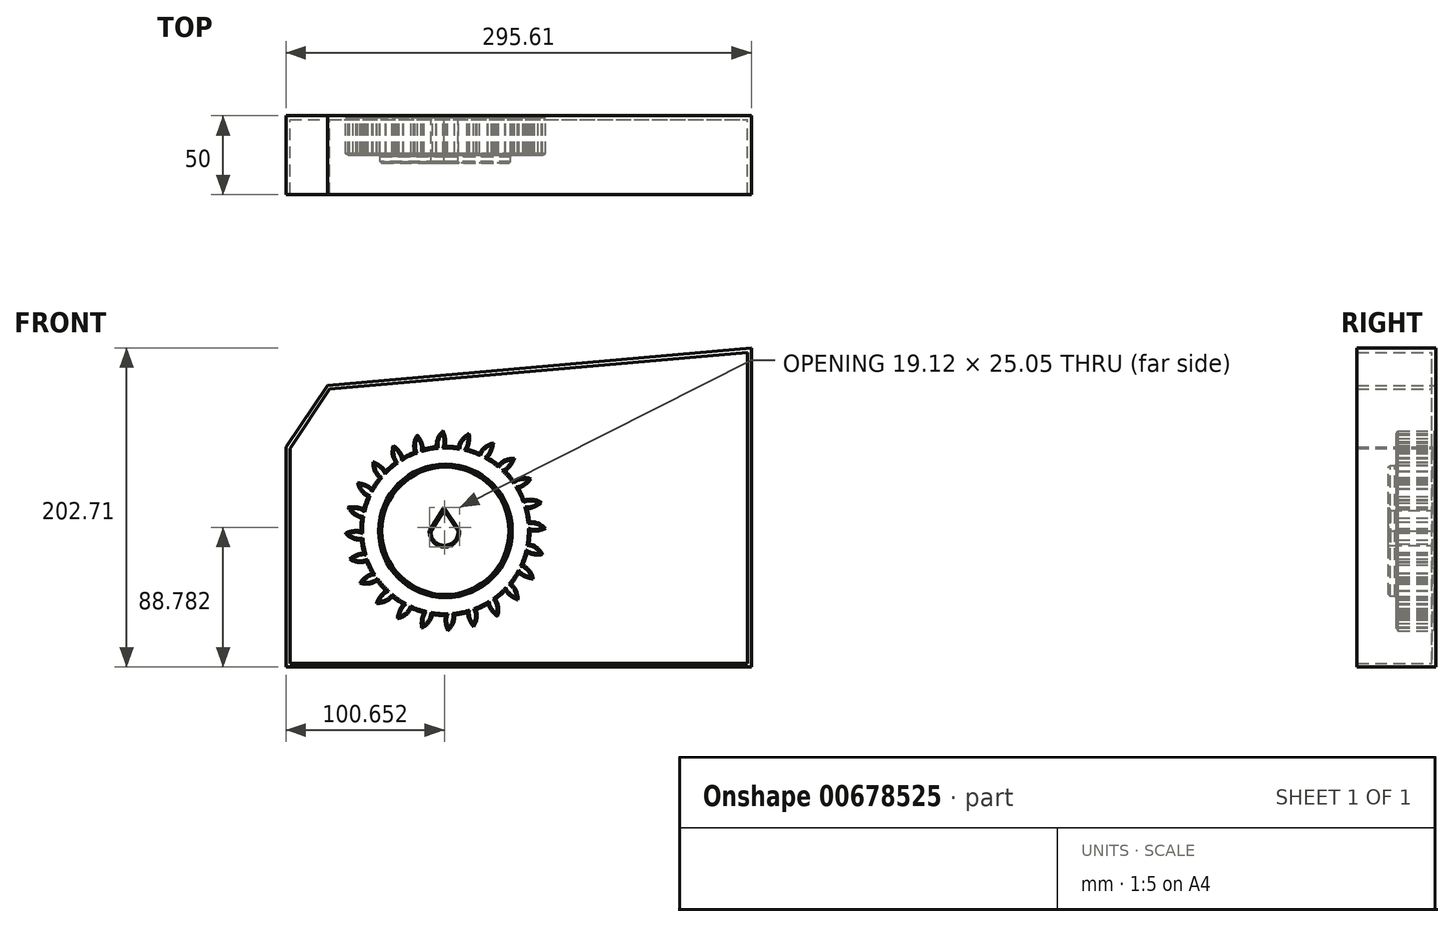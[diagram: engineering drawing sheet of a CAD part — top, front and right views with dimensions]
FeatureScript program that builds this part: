
annotation { "Feature Type Name" : "Feature", "Feature Type Description" : "" }
export const myFeature = defineFeature(function(context is Context, id is Id, definition is map)
    precondition{}
    {
        {
            var Q0;
            Q0=qCreatedBy(makeId("Front.planeOp"),FACE);
            var sketch = newSketch(context, id + "F0", { "sketchPlane" : qUnion([Q0])});
            skCircle(sketch, "E0", {"center": v(0, 0) * mm, "radius": 53.72 * mm});
            skCircle(sketch, "E1", {"center": v(0, 0) * mm, "radius": 58.67 * mm, "construction": true});
            skCircle(sketch, "E2", {"center": v(0, 0) * mm, "radius": 63.5 * mm, "construction": true});
            skLineSegment(sketch, "E3", {"start": v(0, 0) * mm, "end": v(0, 86.11) * mm, "construction": true});
            skLineSegment(sketch, "E4", {"start": v(0, 0) * mm, "end": v(-5.95, 90.7) * mm, "construction": true});
            skCircle(sketch, "E5", {"center": v(0, 58.67) * mm, "radius": 14.6 * mm, "construction": true});
            skLineSegment(sketch, "E6", {"start": v(0, 58.67) * mm, "end": v(-66.92, 58.67) * mm, "construction": true});
            skLineSegment(sketch, "E7", {"start": v(0, 58.67) * mm, "end": v(-68.71, 43.32) * mm, "construction": true});
            skCircle(sketch, "E8", {"center": v(-14.5, 56.86) * mm, "radius": 14.6 * mm, "construction": true});
            skArc(sketch, "E9", {"start": v(0, 58.67) * mm, "mid": v(-0.53, 61.14) * mm, "end": v(-1.48, 63.48) * mm});
            skArc(sketch, "E10", {"start": v(-0.23, 53.72) * mm, "mid": v(0.19, 56.18) * mm, "end": v(0, 58.67) * mm});
            skArc(sketch, "E11", {"start": v(-1.48, 63.48) * mm, "mid": v(-4.9, 58.99) * mm, "end": v(-5.76, 53.41) * mm});
            skCircle(sketch, "E12", {"center": v(0, 0) * mm, "radius": 41.43 * mm});
            skLineSegment(sketch, "E13", {"start": v(-9.22, 0) * mm, "end": v(-0.85, 12.95) * mm});
            skLineSegment(sketch, "E14", {"start": v(-0.85, 12.95) * mm, "end": v(7.96, 0) * mm});
            skArc(sketch, "E15", {"start": v(-9.22, 0) * mm, "mid": v(-0.63, -9.3) * mm, "end": v(7.96, 0) * mm});
            skSolve(sketch);
        }
        {
            var Q0;
            {var subQ0=sQuery(id+"F0.wireOp",EDGE,"E0");var subQ1=makeQuery(id+"F0.imprint","INTERSECT",VERTEX,{"derivedFrom":[subQ0,sQuery(id+"F0.wireOp",EDGE,"E10")]});Q0=makeQuery(id+"F0.imprint","IMPRINT",FACE,{"disambiguationData":[TD([[makeQuery(id+"F0.imprint","IMPRINT",EDGE,{"disambiguationData":[TD([[subQ1,-1.0]])],"derivedFrom":subQ0}),1.0]])]});}
            var Q1;
            Q1=makeQuery(id+"F0.imprint","IMPRINT",FACE,{"disambiguationData":[TD([[makeQuery(id+"F0.imprint","IMPRINT",EDGE,{"derivedFrom":sQuery(id+"F0.wireOp",EDGE,"E9")}),1.0]])]});
            extrude(context, id + "F1", {"entities" : qUnion([Q0, Q1]), "depth" : 25 * mm, "offsetDistance" : 25 * mm});
        }
        {
            var Q0;
            Q0=makeQuery(id+"F1.opExtrude","SWEPT_BODY",BODY,{"disambiguationData":[OSD([sQuery(id+"F0.wireOp",EDGE,"E0"),sQuery(id+"F0.wireOp",EDGE,"E9"),sQuery(id+"F0.wireOp",EDGE,"E10"),sQuery(id+"F0.wireOp",EDGE,"E11")])]});
            var Q1;
            Q1=makeQuery(id+"F1.opExtrude","SWEPT_FACE",FACE,{"disambiguationData":[OSD([sQuery(id+"F0.wireOp",EDGE,"E0")])]});
            circularPattern(context, id + "F2", {"entities" : qUnion([Q0]), "axis" : qUnion([Q1]), "angle" : 360 * degree, "instanceCount" : 24, "equalSpace" : true});
        }
        {
            var Q0;
            Q0=makeQuery(id+"F0.imprint","IMPRINT",FACE,{"disambiguationData":[TD([[makeQuery(id+"F0.imprint","IMPRINT",EDGE,{"derivedFrom":sQuery(id+"F0.wireOp",EDGE,"E12")}),1.0]])]});
            extrude(context, id + "F3", {"entities" : qUnion([Q0]), "operationType" : NewBodyOperationType.ADD, "depth" : 30 * mm, "offsetDistance" : 25 * mm});
        }
        {
            var Q0;
            Q0=makeQuery(id+"F3.opExtrude","CAP_FACE",FACE,{"disambiguationData":[OSD([sQuery(id+"F0.wireOp",EDGE,"E12"),sQuery(id+"F0.wireOp",EDGE,"E13"),sQuery(id+"F0.wireOp",EDGE,"E14"),sQuery(id+"F0.wireOp",EDGE,"E15")])],"isStart":false});
            chamfer(context, id + "F4", {"entities" : qUnion([Q0]), "width" : 1 * mm, "tangentPropagation" : true});
        }
        {
            var Q0;
            {var subQ0=makeQuery(id+"F1.opExtrude","CAP_FACE",FACE,{"disambiguationData":[OSD([sQuery(id+"F0.wireOp",EDGE,"E0"),sQuery(id+"F0.wireOp",EDGE,"E9"),sQuery(id+"F0.wireOp",EDGE,"E10"),sQuery(id+"F0.wireOp",EDGE,"E11"),sQuery(id+"F0.wireOp",EDGE,"E12")])],"isStart":false});Q0=makeQuery(id+"F3.boolean.opBoolean","MERGE",FACE,{"derivedFrom":[subQ0,makeQuery(id+"F2.opPattern","COPY",FACE,{"derivedFrom":subQ0,"instanceName":"1"}),makeQuery(id+"F2.opPattern","COPY",FACE,{"derivedFrom":subQ0,"instanceName":"2"}),makeQuery(id+"F2.opPattern","COPY",FACE,{"derivedFrom":subQ0,"instanceName":"3"}),makeQuery(id+"F2.opPattern","COPY",FACE,{"derivedFrom":subQ0,"instanceName":"4"}),makeQuery(id+"F2.opPattern","COPY",FACE,{"derivedFrom":subQ0,"instanceName":"5"}),makeQuery(id+"F2.opPattern","COPY",FACE,{"derivedFrom":subQ0,"instanceName":"6"}),makeQuery(id+"F2.opPattern","COPY",FACE,{"derivedFrom":subQ0,"instanceName":"7"}),makeQuery(id+"F2.opPattern","COPY",FACE,{"derivedFrom":subQ0,"instanceName":"8"}),makeQuery(id+"F2.opPattern","COPY",FACE,{"derivedFrom":subQ0,"instanceName":"9"}),makeQuery(id+"F2.opPattern","COPY",FACE,{"derivedFrom":subQ0,"instanceName":"10"}),makeQuery(id+"F2.opPattern","COPY",FACE,{"derivedFrom":subQ0,"instanceName":"11"}),makeQuery(id+"F2.opPattern","COPY",FACE,{"derivedFrom":subQ0,"instanceName":"12"}),makeQuery(id+"F2.opPattern","COPY",FACE,{"derivedFrom":subQ0,"instanceName":"13"}),makeQuery(id+"F2.opPattern","COPY",FACE,{"derivedFrom":subQ0,"instanceName":"14"}),makeQuery(id+"F2.opPattern","COPY",FACE,{"derivedFrom":subQ0,"instanceName":"15"}),makeQuery(id+"F2.opPattern","COPY",FACE,{"derivedFrom":subQ0,"instanceName":"16"}),makeQuery(id+"F2.opPattern","COPY",FACE,{"derivedFrom":subQ0,"instanceName":"17"}),makeQuery(id+"F2.opPattern","COPY",FACE,{"derivedFrom":subQ0,"instanceName":"18"}),makeQuery(id+"F2.opPattern","COPY",FACE,{"derivedFrom":subQ0,"instanceName":"19"}),makeQuery(id+"F2.opPattern","COPY",FACE,{"derivedFrom":subQ0,"instanceName":"20"}),makeQuery(id+"F2.opPattern","COPY",FACE,{"derivedFrom":subQ0,"instanceName":"21"}),makeQuery(id+"F2.opPattern","COPY",FACE,{"derivedFrom":subQ0,"instanceName":"22"}),makeQuery(id+"F2.opPattern","COPY",FACE,{"derivedFrom":subQ0,"instanceName":"23"})]});}
            var Q1;
            {var subQ0=sQuery(id+"F0.wireOp",EDGE,"E12");var subQ1=makeQuery(id+"F1.opExtrude","CAP_FACE",FACE,{"disambiguationData":[OSD([sQuery(id+"F0.wireOp",EDGE,"E0"),sQuery(id+"F0.wireOp",EDGE,"E9"),sQuery(id+"F0.wireOp",EDGE,"E10"),sQuery(id+"F0.wireOp",EDGE,"E11"),subQ0])],"isStart":true});Q1=makeQuery(id+"F3.boolean.opBoolean","MERGE",FACE,{"derivedFrom":[subQ1,makeQuery(id+"F2.opPattern","COPY",FACE,{"derivedFrom":subQ1,"instanceName":"1"}),makeQuery(id+"F2.opPattern","COPY",FACE,{"derivedFrom":subQ1,"instanceName":"2"}),makeQuery(id+"F2.opPattern","COPY",FACE,{"derivedFrom":subQ1,"instanceName":"3"}),makeQuery(id+"F2.opPattern","COPY",FACE,{"derivedFrom":subQ1,"instanceName":"4"}),makeQuery(id+"F2.opPattern","COPY",FACE,{"derivedFrom":subQ1,"instanceName":"5"}),makeQuery(id+"F2.opPattern","COPY",FACE,{"derivedFrom":subQ1,"instanceName":"6"}),makeQuery(id+"F2.opPattern","COPY",FACE,{"derivedFrom":subQ1,"instanceName":"7"}),makeQuery(id+"F2.opPattern","COPY",FACE,{"derivedFrom":subQ1,"instanceName":"8"}),makeQuery(id+"F2.opPattern","COPY",FACE,{"derivedFrom":subQ1,"instanceName":"9"}),makeQuery(id+"F2.opPattern","COPY",FACE,{"derivedFrom":subQ1,"instanceName":"10"}),makeQuery(id+"F2.opPattern","COPY",FACE,{"derivedFrom":subQ1,"instanceName":"11"}),makeQuery(id+"F2.opPattern","COPY",FACE,{"derivedFrom":subQ1,"instanceName":"12"}),makeQuery(id+"F2.opPattern","COPY",FACE,{"derivedFrom":subQ1,"instanceName":"13"}),makeQuery(id+"F2.opPattern","COPY",FACE,{"derivedFrom":subQ1,"instanceName":"14"}),makeQuery(id+"F2.opPattern","COPY",FACE,{"derivedFrom":subQ1,"instanceName":"15"}),makeQuery(id+"F2.opPattern","COPY",FACE,{"derivedFrom":subQ1,"instanceName":"16"}),makeQuery(id+"F2.opPattern","COPY",FACE,{"derivedFrom":subQ1,"instanceName":"17"}),makeQuery(id+"F2.opPattern","COPY",FACE,{"derivedFrom":subQ1,"instanceName":"18"}),makeQuery(id+"F2.opPattern","COPY",FACE,{"derivedFrom":subQ1,"instanceName":"19"}),makeQuery(id+"F2.opPattern","COPY",FACE,{"derivedFrom":subQ1,"instanceName":"20"}),makeQuery(id+"F2.opPattern","COPY",FACE,{"derivedFrom":subQ1,"instanceName":"21"}),makeQuery(id+"F2.opPattern","COPY",FACE,{"derivedFrom":subQ1,"instanceName":"22"}),makeQuery(id+"F2.opPattern","COPY",FACE,{"derivedFrom":subQ1,"instanceName":"23"}),makeQuery(id+"F3.opExtrude","CAP_FACE",FACE,{"disambiguationData":[OSD([subQ0,sQuery(id+"F0.wireOp",EDGE,"E13"),sQuery(id+"F0.wireOp",EDGE,"E14"),sQuery(id+"F0.wireOp",EDGE,"E15")])],"isStart":true})]});}
            chamfer(context, id + "F5", {"entities" : qUnion([Q0, Q1]), "width" : 1 * mm, "tangentPropagation" : true});
        }
        {
            var Q0;
            Q0=qCreatedBy(makeId("Front.planeOp"),FACE);
            var sketch = newSketch(context, id + "F6", { "sketchPlane" : qUnion([Q0])});
            skLineSegment(sketch, "E16", {"start": v(-101.28, 53.15) * mm, "end": v(-101.28, -86.55) * mm});
            skLineSegment(sketch, "E17", {"start": v(-101.28, -86.55) * mm, "end": v(194.33, -86.55) * mm});
            skLineSegment(sketch, "E18", {"start": v(194.33, -86.55) * mm, "end": v(194.33, 116.16) * mm});
            skLineSegment(sketch, "E19", {"start": v(-101.28, 53.15) * mm, "end": v(-74.95, 92.45) * mm});
            skLineSegment(sketch, "E20", {"start": v(-74.95, 92.45) * mm, "end": v(194.33, 116.16) * mm});
            skSolve(sketch);
        }
        {
            var Q0;
            Q0=makeQuery(id+"F6.imprint","IMPRINT",FACE,{"disambiguationData":[TD([[makeQuery(id+"F6.imprint","IMPRINT",EDGE,{"derivedFrom":sQuery(id+"F6.wireOp",EDGE,"E16")}),1.0]])]});
            extrude(context, id + "F7", {"entities" : qUnion([Q0]), "depth" : 50 * mm, "offsetDistance" : 25 * mm});
        }
        {
            var Q0;
            Q0=makeQuery(id+"F7.opExtrude","CAP_FACE",FACE,{"disambiguationData":[OSD([sQuery(id+"F6.wireOp",EDGE,"E16"),sQuery(id+"F6.wireOp",EDGE,"E17"),sQuery(id+"F6.wireOp",EDGE,"E18"),sQuery(id+"F6.wireOp",EDGE,"E19"),sQuery(id+"F6.wireOp",EDGE,"E20")])],"isStart":false});
            shell(context, id + "F8", {"entities" : qUnion([Q0]), "thickness" : 2.5 * mm});
        }
    });
